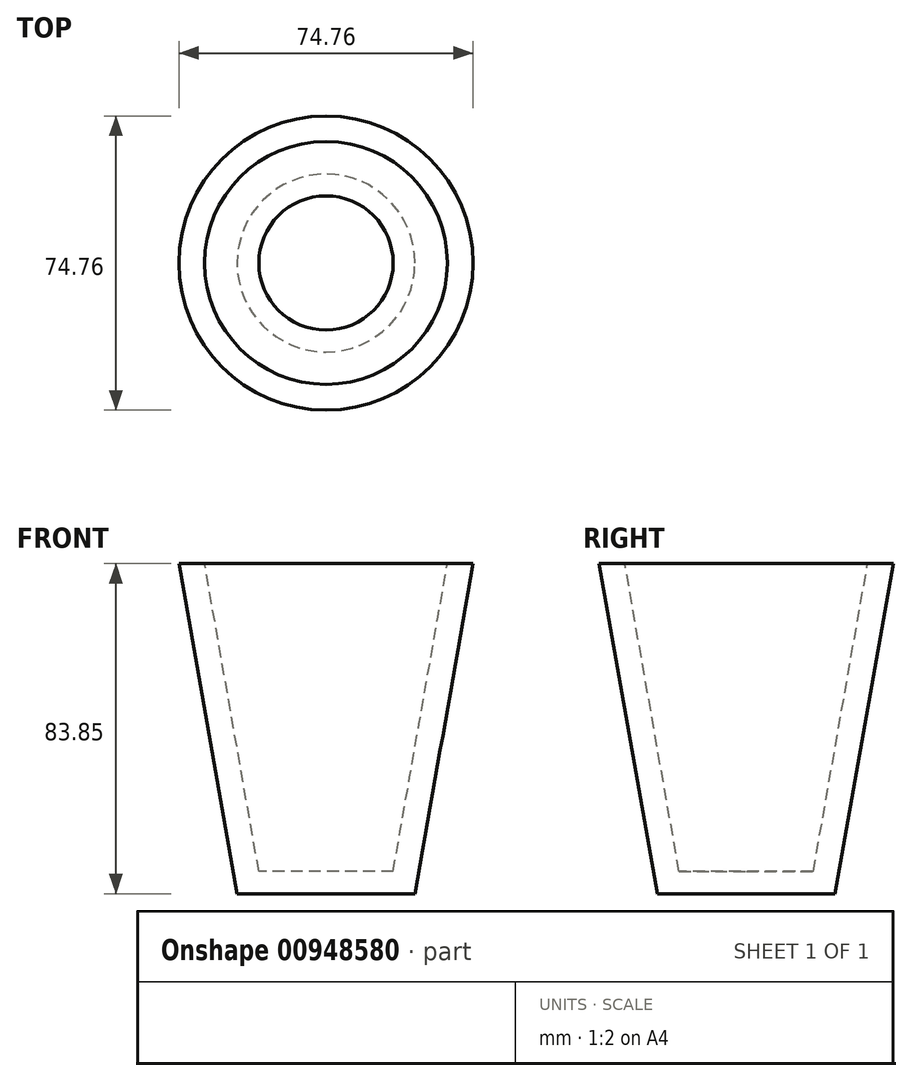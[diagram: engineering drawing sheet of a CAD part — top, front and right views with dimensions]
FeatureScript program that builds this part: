
annotation { "Feature Type Name" : "Feature", "Feature Type Description" : "" }
export const myFeature = defineFeature(function(context is Context, id is Id, definition is map)
    precondition{}
    {
        {
            var Q0;
            Q0=qCreatedBy(makeId("Front.planeOp"),FACE);
            var sketch = newSketch(context, id + "F0", { "sketchPlane" : qUnion([Q0])});
            skLineSegment(sketch, "E0", {"start": v(-37.38, 45.76) * mm, "end": v(-22.6, -38.09) * mm});
            skLineSegment(sketch, "E1", {"start": v(-22.6, -38.09) * mm, "end": v(0, -38.09) * mm});
            skLineSegment(sketch, "E2", {"start": v(-37.38, 45.76) * mm, "end": v(-30.84, 45.76) * mm});
            skLineSegment(sketch, "E3", {"start": v(-30.84, 45.76) * mm, "end": v(-17.06, -32.41) * mm});
            skLineSegment(sketch, "E4", {"start": v(-17.06, -32.41) * mm, "end": v(0, -32.41) * mm});
            skLineSegment(sketch, "E5", {"start": v(0, -32.41) * mm, "end": v(0, -38.09) * mm});
            skSolve(sketch);
        }
        {
            var Q0;
            Q0=makeQuery(id+"F0.imprint","IMPRINT",FACE,{"disambiguationData":[TD([[makeQuery(id+"F0.imprint","IMPRINT",EDGE,{"derivedFrom":sQuery(id+"F0.wireOp",EDGE,"E0")}),1.0]])]});
            var Q1;
            Q1=sQuery(id+"F0.wireOp",EDGE,"E5");
            revolve(context, id + "F1", {"surfaceOperationType" : NewSurfaceOperationType.NEW, "entities" : qUnion([Q0]), "axis" : qUnion([Q1]), "revolveType" : RevolveType.FULL});
        }
    });
